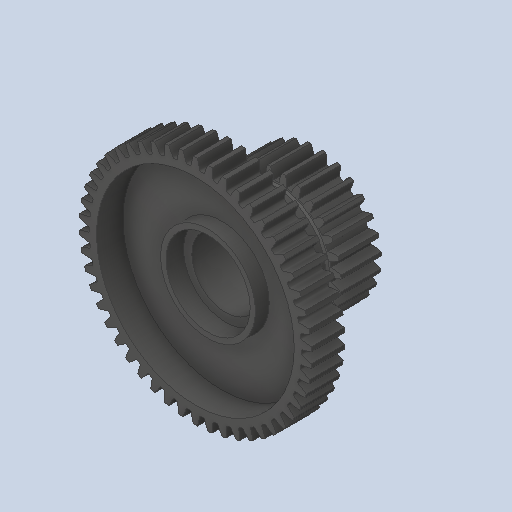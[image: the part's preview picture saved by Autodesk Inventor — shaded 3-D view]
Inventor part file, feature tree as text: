
AUTODESK INVENTOR PART (.ipt)
format: ipt  version: 2023.4 (Build 274418000, 418)  size: 580,096 bytes
history: native  units: in
note: dims shown in document units (in); Inventor stores cm internally (conversion verified against a paired STEP export)
features: chamfer x1
ambient origin geometry x8: Origin, YZ Plane, XZ Plane, XY Plane, X Axis, Y Axis, Z Axis, Center Point
bodies: Solid1 (feature_tree)
feature tree (1):
  chamfer  "Chamfer2"  [1 undecoded]
note: 1 required parameter value undecoded (feature->parameter linkage not recoverable at this tier; creation-order binding heuristic only, values carry confidence <= 0.55)
